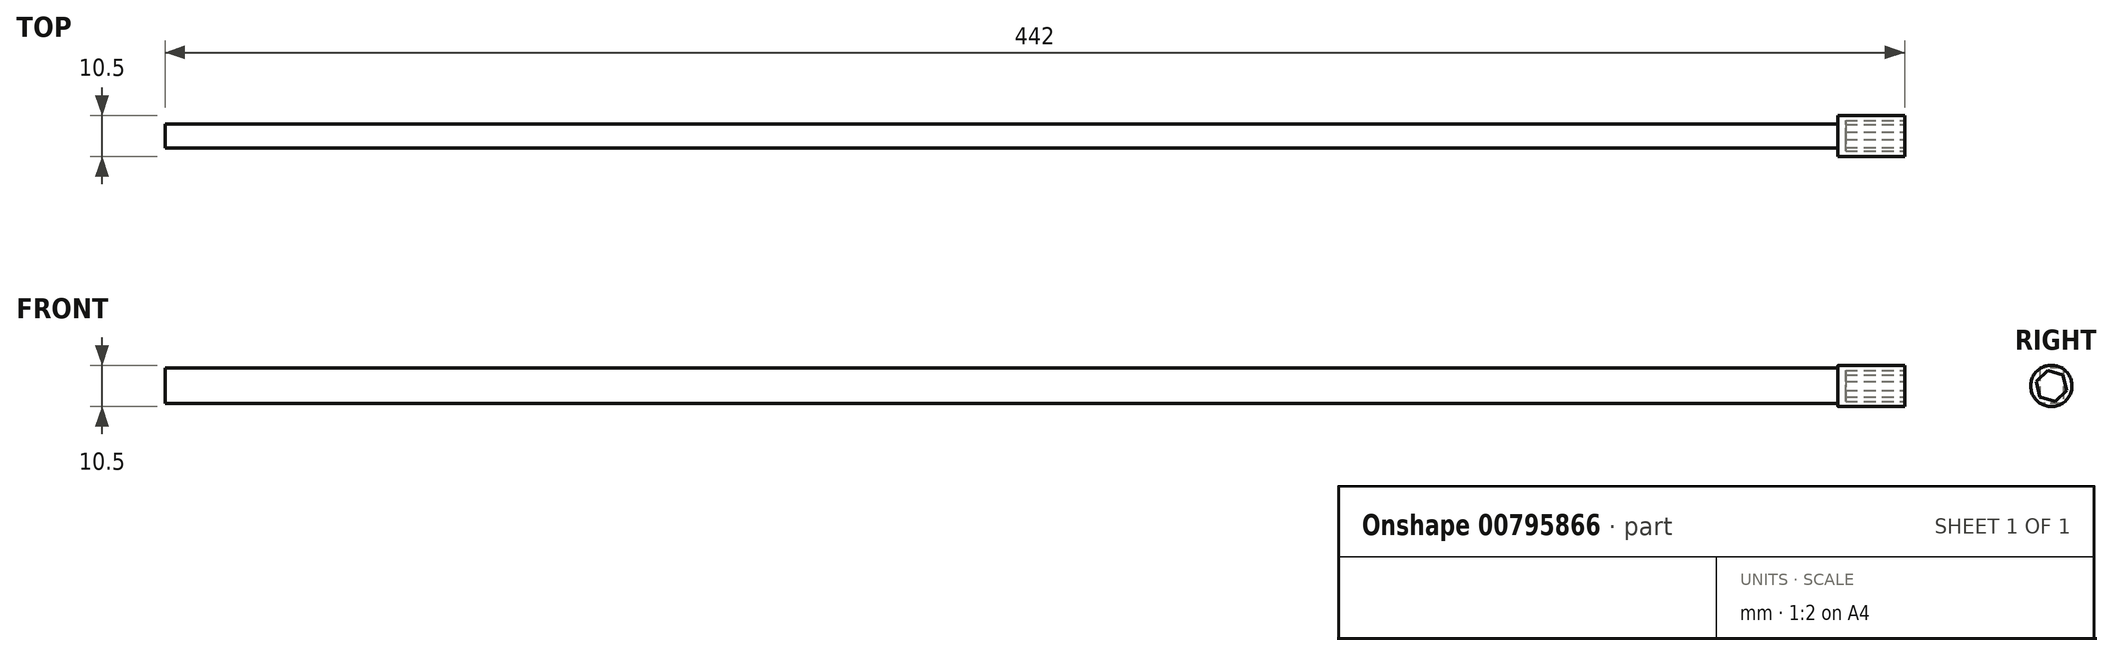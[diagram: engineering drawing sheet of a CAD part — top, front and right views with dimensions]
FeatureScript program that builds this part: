
annotation { "Feature Type Name" : "Feature", "Feature Type Description" : "" }
export const myFeature = defineFeature(function(context is Context, id is Id, definition is map)
    precondition{}
    {
        {
            var Q0;
            Q0=qCreatedBy(makeId("Top.planeOp"),FACE);
            var sketch = newSketch(context, id + "F0", { "sketchPlane" : qUnion([Q0])});
            skLineSegment(sketch, "E0", {"start": v(-32.5, 0) * mm, "end": v(32.24, 0) * mm, "construction": true});
            skLineSegment(sketch, "E1.bottom", {"start": v(-29.27, 3) * mm, "end": v(395.73, 3) * mm});
            skLineSegment(sketch, "E1.top", {"start": v(-29.27, -3) * mm, "end": v(395.73, -3) * mm});
            skLineSegment(sketch, "E1.left", {"start": v(-29.27, 3) * mm, "end": v(-29.27, -3) * mm});
            skLineSegment(sketch, "E1.right", {"start": v(395.73, 3) * mm, "end": v(395.73, -3) * mm});
            skSolve(sketch);
        }
        {
            var Q0;
            Q0 = qSketchRegion(id + "F0", true);
            extrude(context, id + "F1", {"entities" : qUnion([Q0]), "depth" : 9 * mm, "offsetDistance" : 25 * mm});
        }
        {
            var Q0;
            Q0=makeQuery(id+"F1.opExtrude","SWEPT_FACE",FACE,{"disambiguationData":[OSD([sQuery(id+"F0.wireOp",EDGE,"E1.right")])]});
            var sketch = newSketch(context, id + "F2", { "sketchPlane" : qUnion([Q0])});
            skCircle(sketch, "E2", {"center": v(0, 4.5) * mm, "radius": 5.25 * mm});
            skSolve(sketch);
        }
        {
            var Q0;
            Q0 = qSketchRegion(id + "F2", true);
            extrude(context, id + "F3", {"entities" : qUnion([Q0]), "operationType" : NewBodyOperationType.ADD, "depth" : 17 * mm, "offsetDistance" : 25 * mm});
        }
        {
            var Q0;
            Q0=makeQuery(id+"F3.opExtrude","CAP_FACE",FACE,{"disambiguationData":[OSD([sQuery(id+"F2.wireOp",EDGE,"E2")])],"isStart":false});
            var sketch = newSketch(context, id + "F4", { "sketchPlane" : qUnion([Q0])});
            skCircle(sketch, "E3.cCircle", {"center": v(0, 4.5) * mm, "radius": 3.5 * mm, "construction": true});
            skLineSegment(sketch, "E3.0", {"start": v(3.88, 3.36) * mm, "end": v(0.95, 0.57) * mm});
            skLineSegment(sketch, "E3.1", {"start": v(0.95, 0.57) * mm, "end": v(-2.92, 1.7) * mm});
            skLineSegment(sketch, "E3.2", {"start": v(-2.92, 1.7) * mm, "end": v(-3.88, 5.64) * mm});
            skLineSegment(sketch, "E3.3", {"start": v(-3.88, 5.64) * mm, "end": v(-0.95, 8.43) * mm});
            skLineSegment(sketch, "E3.4", {"start": v(-0.95, 8.43) * mm, "end": v(2.92, 7.3) * mm});
            skLineSegment(sketch, "E3.5", {"start": v(2.92, 7.3) * mm, "end": v(3.88, 3.36) * mm});
            skPoint(sketch, "E3.0.midPoint", {"position": v(2.42, 1.97) * mm});
            skSolve(sketch);
        }
        {
            var Q0;
            Q0 = qSketchRegion(id + "F4", true);
            extrude(context, id + "F5", {"entities" : qUnion([Q0]), "operationType" : NewBodyOperationType.REMOVE, "oppositeDirection" : true, "depth" : 15 * mm, "offsetDistance" : 25 * mm});
        }
    });
